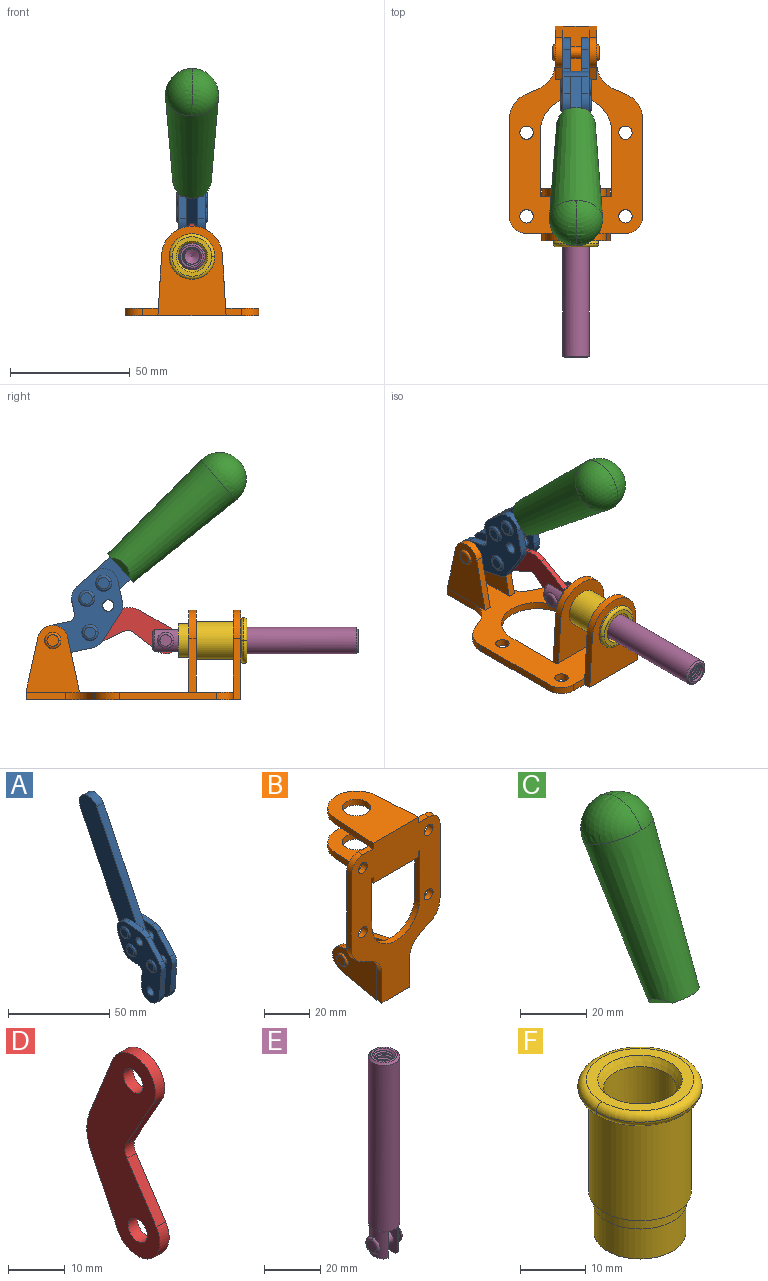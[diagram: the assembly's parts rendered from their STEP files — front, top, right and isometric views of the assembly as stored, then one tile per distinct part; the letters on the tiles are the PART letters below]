
ASSEMBLY  parts=6 mates=6
PART A: 59 faces, bbox 12.9x60.2x99.6 mm
  f0: torus R=2.39mm, axis (-1,0,0), area 14.9mm2, adj f20,f43,f51
  f1: torus R=2.39mm, axis (-1,0,0), area 14.9mm2, adj f19,f42,f51
  f2: torus R=2.39mm, axis (-1,0,0), area 14.9mm2, adj f18,f35,f51
  f3: torus R=2.39mm, axis (-1,0,0), area 14.9mm2, adj f14,f17,f23
  f4: torus R=2.39mm, axis (-1,0,0), area 14.9mm2, adj f13,f16,f23
  f5: torus R=2.39mm, axis (-1,0,0), area 14.9mm2, adj f12,f15,f23
  f6: cylinder r=2.39mm len=4.78mm, axis (1,0,0), area 46.5mm2, adj f48,f50,f51
  f7: cylinder r=2.39mm len=4.78mm, axis (1,0,0), area 46.5mm2, adj f50,f51
  f8: cylinder r=6.35mm len=12.68mm, axis (1,0,0), area 61.8mm2, adj f38,f39,f50,f51
  f9: cylinder r=2.39mm len=4.78mm, axis (-1,0,0), area 70.5mm2, adj f46,f50
  f10: cylinder r=2.39mm len=4.78mm, axis (-1,0,0), area 46.5mm2, adj f23,f45,f46
  f11: cylinder r=2.39mm len=4.78mm, axis (-1,0,0), area 46.5mm2, adj f23,f46
  f12: plane 4.78x4.78mm, normal (1,0,0), area 17.9mm2, adj f5,f15
  f13: plane 4.78x4.78mm, normal (1,0,0), area 17.9mm2, adj f4,f16
  f14: plane 4.78x4.78mm, normal (1,0,0), area 17.9mm2, adj f3,f17
  f15: torus R=2.39mm, axis (-1,0,0), area 14.9mm2, adj f5,f12,f23
  f16: torus R=2.39mm, axis (-1,0,0), area 14.9mm2, adj f4,f13,f23
  f17: torus R=2.39mm, axis (-1,0,0), area 14.9mm2, adj f3,f14,f23
  f18: plane 4.78x4.78mm, normal (-1,0,0), area 17.9mm2, adj f2,f35
  f19: plane 4.78x4.78mm, normal (-1,0,0), area 17.9mm2, adj f1,f42
  f20: plane 4.78x4.78mm, normal (-1,0,0), area 17.9mm2, adj f0,f43
  f21: plane 2.26x0.2mm, normal (1,0,0), area 0.2mm2, adj f31,f44
  f22: plane 2.26x0.2mm, normal (-1,0,0), area 0.2mm2, adj f41,f44
  f23: plane 39.37x30.77mm, normal (1,0,0), area 565.5mm2, adj f3,f4,f5,f10,f11,f15,f16,f17
  f24: cylinder r=6.1mm len=4.15mm, axis (-1,0,0), area 14.7mm2, adj f23,f25,f32,f46
  f25: plane 10.25x9.01mm, normal (0,-0.75,0.66), area 42.3mm2, adj f23,f24,f26,f46
  f26: cylinder r=6.35mm len=4.64mm, axis (-1,0,0), area 15.6mm2, adj f23,f25,f27,f46
  f27: plane 15.84x3.1mm, normal (0,-1,-0.07), area 49.2mm2, adj f23,f26,f28,f46
  f28: cylinder r=6.35mm len=12.68mm, axis (-1,0,0), area 61.8mm2, adj f23,f27,f29,f46
  f29: plane 8.11x3.1mm, normal (0,1,0.07), area 25.2mm2, adj f23,f28,f30,f46
  f30: cylinder r=3.05mm len=3.25mm, axis (-1,0,0), area 14.8mm2, adj f23,f29,f31,f46
  f31: plane 5.99x3.1mm, normal (0,0.07,-1), area 18.6mm2, adj f21,f23,f30,f44,f46
  f32: plane 9.5x3.1mm, normal (0,-0.07,1), area 29.5mm2, adj f23,f24,f33,f46,f47
  f33: cylinder r=6.1mm len=8.63mm, axis (-1,0,0), area 39.1mm2, adj f23,f32,f34,f47
  f34: plane 8.65x3.96mm, normal (0,0.91,-0.42), area 29.5mm2, adj f23,f33,f44,f47
  f35: torus R=2.39mm, axis (-1,0,0), area 14.9mm2, adj f2,f18,f51
  f36: plane 10.25x9.01mm, normal (0,-0.75,0.66), area 42.3mm2, adj f37,f49,f50,f51
  f37: cylinder r=6.35mm len=4.64mm, axis (1,0,0), area 15.6mm2, adj f36,f38,f50,f51
  f38: plane 15.84x3.1mm, normal (0,-1,-0.07), area 49.2mm2, adj f8,f37,f50,f51
  f39: plane 8.11x3.1mm, normal (0,1,0.07), area 25.2mm2, adj f8,f40,f50,f51
  f40: cylinder r=3.05mm len=3.25mm, axis (1,0,0), area 14.8mm2, adj f39,f41,f50,f51
  f41: plane 5.99x3.1mm, normal (0,0.07,-1), area 18.6mm2, adj f22,f40,f44,f50,f51
  f42: torus R=2.39mm, axis (-1,0,0), area 14.9mm2, adj f1,f19,f51
  f43: torus R=2.39mm, axis (-1,0,0), area 14.9mm2, adj f0,f20,f51
  f44: cylinder r=6.35mm len=12.12mm, axis (-1,0,0), area 128.9mm2, adj f21,f22,f23,f31,f34,f41,f46,f47
  f45: plane 2.65x1.35mm, normal (1,0,0), area 1mm2, adj f10,f55
  f46: plane 39.08x20.42mm, normal (-1,0,0), area 412.5mm2, adj f9,f10,f11,f24,f25,f26,f27,f28
  f47: plane 77.62x39.82mm, normal (1,0,0), area 850mm2, adj f32,f33,f34,f44,f53,f54,f55
  f48: plane 2.65x1.35mm, normal (-1,0,0), area 1mm2, adj f6,f55
  f49: cylinder r=6.1mm len=4.15mm, axis (1,0,0), area 14.7mm2, adj f36,f50,f51,f56
  f50: plane 39.08x20.42mm, normal (1,0,0), area 412.5mm2, adj f6,f7,f8,f9,f36,f37,f38,f39
  f51: plane 39.37x30.77mm, normal (-1,0,0), area 565.5mm2, adj f0,f1,f2,f6,f7,f8,f35,f36
  f52: plane 8.65x3.96mm, normal (0,0.91,-0.42), area 29.5mm2, adj f44,f51,f57,f58
  f53: plane 68.49x33.4mm, normal (0,0.9,-0.44), area 358.1mm2, adj f44,f47,f54,f58
  f54: cylinder r=6.35mm len=12.06mm, axis (1,0,0), area 93.7mm2, adj f47,f53,f55,f58
  f55: plane 68.49x33.4mm, normal (0,-0.9,0.44), area 358.1mm2, adj f44,f45,f46,f47,f48,f50,f54,f58
  f56: plane 9.5x3.1mm, normal (0,-0.07,1), area 29.5mm2, adj f49,f50,f51,f57,f58
  f57: cylinder r=6.1mm len=8.63mm, axis (1,0,0), area 39.1mm2, adj f51,f52,f56,f58
  f58: plane 77.62x39.82mm, normal (-1,0,0), area 850mm2, adj f44,f52,f53,f54,f55,f56,f57
PART B: 55 faces, bbox 55.7x37.4x89.8 mm
  f0: torus R=2.41mm, axis (-1,0,0), area 15mm2, adj f11,f15,f25
  f1: torus R=2.41mm, axis (-1,0,0), area 15mm2, adj f10,f12,f22
  f2: cylinder r=2.78mm len=5.56mm, axis (0,-1,0), area 54.2mm2, adj f30,f54
  f3: cylinder r=14.99mm len=29.97mm, axis (0,-1,0), area 145.9mm2, adj f30,f49,f53,f54
  f4: cylinder r=2.78mm len=5.56mm, axis (0,-1,0), area 54.2mm2, adj f30,f54
  f5: cylinder r=2.78mm len=5.56mm, axis (0,-1,0), area 54.2mm2, adj f30,f54
  f6: cylinder r=2.78mm len=5.56mm, axis (0,-1,0), area 54.2mm2, adj f30,f54
  f7: cylinder r=6.35mm len=12.7mm, axis (0,0,1), area 123.6mm2, adj f27,f51
  f8: cylinder r=6.35mm len=12.7mm, axis (0,0,-1), area 124.7mm2, adj f21,f35
  f9: cylinder r=2.41mm len=11.18mm, axis (-1,0,0), area 169.4mm2, adj f16,f19
  f10: plane 4.83x4.83mm, normal (1,0,0), area 18.3mm2, adj f1,f12
  f11: plane 4.83x4.83mm, normal (-1,0,0), area 18.3mm2, adj f0,f15
  f12: torus R=2.41mm, axis (-1,0,0), area 15mm2, adj f1,f10,f22
  f13: cylinder r=6.35mm len=12.41mm, axis (1,0,0), area 53.4mm2, adj f18,f19,f22,f23
  f14: cylinder r=6.35mm len=12.41mm, axis (-1,0,0), area 53.4mm2, adj f16,f17,f24,f25
  f15: torus R=2.41mm, axis (-1,0,0), area 15mm2, adj f0,f11,f25
  f16: plane 27.86x22.35mm, normal (1,0,0), area 425.4mm2, adj f9,f14,f17,f24,f30
  f17: plane 22.86x4.97mm, normal (0,0.21,0.98), area 72.5mm2, adj f14,f16,f25,f30
  f18: plane 22.86x4.97mm, normal (0,0.21,0.98), area 72.5mm2, adj f13,f19,f22,f30
  f19: plane 27.86x22.35mm, normal (-1,0,0), area 425.4mm2, adj f9,f13,f18,f23,f30
  f20: cylinder r=12.7mm len=25.35mm, axis (0,0,-1), area 119.8mm2, adj f21,f34,f35,f36
  f21: plane 34.21x28.07mm, normal (0,0,-1), area 702.4mm2, adj f8,f20,f30,f34,f36
  f22: plane 27.96x22.45mm, normal (1,0,0), area 407.2mm2, adj f1,f12,f13,f18,f23,f30,f42,f43
  f23: plane 22.86x4.97mm, normal (0,0.21,-0.98), area 72.5mm2, adj f13,f19,f22,f44
  f24: plane 22.86x4.97mm, normal (0,0.21,-0.98), area 72.5mm2, adj f14,f16,f25,f44
  f25: plane 27.86x22.35mm, normal (-1,0,0), area 407.1mm2, adj f0,f14,f15,f17,f24,f30,f45,f46
  f26: plane 3.1x0.95mm, normal (0,0,-1), area 2.7mm2, adj f30,f49,f50,f54
  f27: plane 34.21x28.07mm, normal (0,0,1), area 702.4mm2, adj f7,f28,f30,f50,f52
  f28: cylinder r=12.7mm len=25.35mm, axis (0,0,1), area 118.8mm2, adj f27,f50,f51,f52
  f29: plane 3.1x0.95mm, normal (0,0,-1), area 2.7mm2, adj f30,f52,f53,f54
  f30: plane 86.54x55.63mm, normal (0,1,0), area 2362.9mm2, adj f2,f3,f4,f5,f6,f16,f17,f18
  f31: plane 40.56x3.1mm, normal (-1,0,0), area 125.7mm2, adj f30,f32,f48,f54
  f32: cylinder r=7.11mm len=7.11mm, axis (0,-1,0), area 34.6mm2, adj f30,f31,f33,f54
  f33: plane 6.67x3.1mm, normal (0,0,1), area 20.4mm2, adj f30,f32,f34,f54
  f34: plane 25.39x3.13mm, normal (-1,0.06,0), area 79.5mm2, adj f20,f21,f33,f35,f54
  f35: plane 37.31x28.45mm, normal (0,0,1), area 789.9mm2, adj f8,f20,f34,f36,f54
  f36: plane 25.39x3.13mm, normal (1,0.06,0), area 79.5mm2, adj f20,f21,f35,f37,f54
  f37: plane 6.67x3.1mm, normal (0,0,1), area 20.4mm2, adj f30,f36,f38,f54
  f38: cylinder r=7.11mm len=7.11mm, axis (0,-1,0), area 34.6mm2, adj f30,f37,f39,f54
  f39: plane 40.56x3.1mm, normal (1,0,0), area 125.7mm2, adj f30,f38,f40,f54
  f40: cylinder r=11.18mm len=10.16mm, axis (0,-1,0), area 39.5mm2, adj f30,f39,f41,f54
  f41: plane 6.09x3.1mm, normal (0.42,0,-0.91), area 20.8mm2, adj f30,f40,f42,f54
  f42: cylinder r=11.18mm len=9.41mm, axis (0,-1,0), area 37.2mm2, adj f22,f30,f41,f43,f54
  f43: plane 16.5x3.1mm, normal (1,0,0), area 51.1mm2, adj f22,f42,f44,f54
  f44: plane 17.37x3.1mm, normal (0,0,-1), area 53.8mm2, adj f23,f24,f30,f43,f45,f54
  f45: plane 16.5x3.1mm, normal (-1,0,0), area 51.1mm2, adj f25,f44,f46,f54
  f46: cylinder r=11.18mm len=9.41mm, axis (0,-1,0), area 37.2mm2, adj f25,f30,f45,f47,f54
  f47: plane 6.09x3.1mm, normal (-0.42,0,-0.91), area 20.8mm2, adj f30,f46,f48,f54
  f48: cylinder r=11.18mm len=10.16mm, axis (0,-1,0), area 39.5mm2, adj f30,f31,f47,f54
  f49: plane 26.54x3.1mm, normal (-1,0,0), area 82.3mm2, adj f3,f26,f30,f54
  f50: plane 25.39x3.1mm, normal (1,0.06,0), area 78.8mm2, adj f26,f27,f28,f51,f54
  f51: plane 37.31x28.45mm, normal (0,0,-1), area 789.9mm2, adj f7,f28,f50,f52,f54
  f52: plane 25.39x3.1mm, normal (-1,0.06,0), area 78.8mm2, adj f27,f28,f29,f51,f54
  f53: plane 26.54x3.1mm, normal (1,0,0), area 82.3mm2, adj f3,f29,f30,f54
  f54: plane 89.66x55.63mm, normal (0,-1,0), area 2678.5mm2, adj f2,f3,f4,f5,f6,f26,f29,f31
PART C: 11 faces, bbox 22.3x42.6x64.5 mm
  f0: sphere r=11.13mm, area 411.4mm2, adj f1,f8
  f1: cone r=11.11mm half-angle=3.3deg, axis (0,0.44,0.9), area 3251.8mm2, adj f0,f7,f8,f9,f10
  f2: cylinder r=6.16mm len=11.7mm, axis (1,0,0), area 89.5mm2, adj f3,f4,f5,f6
  f3: plane 60.23x36.75mm, normal (-1,0,0), area 763.6mm2, adj f2,f4,f6,f10
  f4: plane 51.37x25.05mm, normal (0,0.9,-0.44), area 264.2mm2, adj f2,f3,f5,f10
  f5: plane 60.23x36.75mm, normal (1,0,0), area 763.6mm2, adj f2,f4,f6,f10
  f6: plane 51.37x25.05mm, normal (0,-0.9,0.44), area 264.2mm2, adj f2,f3,f5,f10
  f7: plane 9.95x5.95mm, normal (0.71,-0.31,-0.64), area 25.8mm2, adj f1,f10
  f8: sphere r=11.13mm, area 411.4mm2, adj f0,f1
  f9: plane 9.95x5.95mm, normal (-0.71,-0.31,-0.64), area 25.8mm2, adj f1,f10
  f10: plane 14.27x11.38mm, normal (0,-0.44,-0.9), area 106.7mm2, adj f1,f3,f4,f5,f6,f7,f9
PART D: 12 faces, bbox 2.3x18.2x42.8 mm
  f0: cylinder r=2.4mm len=4.8mm, axis (1,0,0), area 34.9mm2, adj f4,f11
  f1: cylinder r=10.41mm len=8.47mm, axis (1,0,0), area 20.2mm2, adj f4,f9,f10,f11
  f2: cylinder r=3.05mm len=3.16mm, axis (1,0,0), area 7.7mm2, adj f4,f6,f7,f11
  f3: cylinder r=2.4mm len=4.8mm, axis (1,0,0), area 34.9mm2, adj f4,f11
  f4: plane 42.81x18.23mm, normal (-1,0,0), area 414.1mm2, adj f0,f1,f2,f3,f5,f6,f7,f8
  f5: cylinder r=5.54mm len=10.67mm, axis (1,0,0), area 41.8mm2, adj f4,f6,f10,f11
  f6: plane 11.66x6.53mm, normal (0,-0.87,-0.49), area 30.9mm2, adj f2,f4,f5,f11
  f7: plane 11.17x7.33mm, normal (0,-0.84,0.55), area 30.9mm2, adj f2,f4,f8,f11
  f8: cylinder r=5.54mm len=10.51mm, axis (1,0,0), area 41.8mm2, adj f4,f7,f9,f11
  f9: plane 13.67x6.67mm, normal (0,0.9,-0.44), area 35.1mm2, adj f1,f4,f8,f11
  f10: plane 14.1x5.7mm, normal (0,0.93,0.37), area 35.1mm2, adj f1,f4,f5,f11
  f11: plane 42.81x18.23mm, normal (1,0,0), area 414.1mm2, adj f0,f1,f2,f3,f5,f6,f7,f8
PART E: 48 faces, bbox 12.6x11.1x86.1 mm
  f0: torus R=2.41mm, axis (-1,0,0), area 15mm2, adj f30,f32,f34
  f1: torus R=2.41mm, axis (-1,0,0), area 15mm2, adj f29,f31,f33
  f2: cylinder r=5.54mm len=72.39mm, axis (0,0,1), area 2518.5mm2, adj f3,f4,f42,f43
  f3: cone r=5.54mm half-angle=45deg, axis (0,0,1), area 7.6mm2, adj f2,f5,f41
  f4: cone r=5.54mm half-angle=45deg, axis (0,0,-1), area 34.9mm2, adj f2,f39
  f5: cylinder r=5.08mm len=11.48mm, axis (0,0,1), area 108.3mm2, adj f3,f7,f8,f41
  f6: cylinder r=2.41mm len=4.83mm, axis (-1,0,0), area 71.2mm2, adj f40,f41
  f7: cylinder r=2.41mm len=4.83mm, axis (-1,0,0), area 7.6mm2, adj f5,f34
  f8: cone r=5.08mm half-angle=45deg, axis (0,0,1), area 10.6mm2, adj f5,f37,f41
  f9: cone r=3.98mm half-angle=45deg, axis (0,0,1), area 17.6mm2, adj f27,f39,f45,f46,f47
  f10: cylinder r=2.41mm len=4.83mm, axis (-1,0,0), area 7.6mm2, adj f33,f38
  f11: cylinder r=3.2mm len=6.4mm, axis (0,0,1), area 78.4mm2, adj f12,f28,f44,f45,f47
  f12: cylinder r=3.2mm len=6.4mm, axis (0,0,1), area 10.5mm2, adj f11,f13,f45,f47
  f13: cylinder r=3.2mm len=6.4mm, axis (0,0,1), area 10.5mm2, adj f12,f14,f45,f47
  f14: cylinder r=3.2mm len=6.4mm, axis (0,0,1), area 10.5mm2, adj f13,f15,f45,f47
  f15: cylinder r=3.2mm len=6.4mm, axis (0,0,1), area 10.5mm2, adj f14,f16,f45,f47
  f16: cylinder r=3.2mm len=6.4mm, axis (0,0,1), area 10.5mm2, adj f15,f17,f45,f47
  f17: cylinder r=3.2mm len=6.4mm, axis (0,0,1), area 10.5mm2, adj f16,f18,f45,f47
  f18: cylinder r=3.2mm len=6.4mm, axis (0,0,1), area 10.5mm2, adj f17,f19,f45,f47
  f19: cylinder r=3.2mm len=6.4mm, axis (0,0,1), area 10.5mm2, adj f18,f20,f45,f47
  f20: cylinder r=3.2mm len=6.4mm, axis (0,0,1), area 10.5mm2, adj f19,f21,f45,f47
  f21: cylinder r=3.2mm len=6.4mm, axis (0,0,1), area 10.5mm2, adj f20,f22,f45,f47
  f22: cylinder r=3.2mm len=6.4mm, axis (0,0,1), area 10.5mm2, adj f21,f23,f45,f47
  f23: cylinder r=3.2mm len=6.4mm, axis (0,0,1), area 10.5mm2, adj f22,f24,f45,f47
  f24: cylinder r=3.2mm len=6.4mm, axis (0,0,1), area 10.5mm2, adj f23,f25,f45,f47
  f25: cylinder r=3.2mm len=6.4mm, axis (0,0,1), area 10.5mm2, adj f24,f26,f45,f47
  f26: cylinder r=3.2mm len=6.4mm, axis (0,0,1), area 10.5mm2, adj f25,f27,f45,f47
  f27: cylinder r=3.2mm len=6.4mm, axis (0,0,1), area 7.4mm2, adj f9,f26,f45,f47
  f28: cone r=3.2mm half-angle=60deg, axis (0,0,1), area 37.2mm2, adj f11
  f29: plane 4.83x4.83mm, normal (-1,0,0), area 18.3mm2, adj f1,f31
  f30: plane 4.83x4.83mm, normal (1,0,0), area 18.3mm2, adj f0,f32
  f31: torus R=2.41mm, axis (-1,0,0), area 15mm2, adj f1,f29,f33
  f32: torus R=2.41mm, axis (-1,0,0), area 15mm2, adj f0,f30,f34
  f33: plane 6.83x6.83mm, normal (1,0,0), area 18.3mm2, adj f1,f10,f31
  f34: plane 6.83x6.83mm, normal (-1,0,0), area 18.3mm2, adj f0,f7,f32
  f35: cone r=5.08mm half-angle=45deg, axis (0,0,1), area 10.6mm2, adj f36,f38,f40
  f36: plane 7.25x1.97mm, normal (0,0,-1), area 10mm2, adj f35,f40
  f37: plane 7.25x1.97mm, normal (0,0,-1), area 10mm2, adj f8,f41
  f38: cylinder r=5.08mm len=11.48mm, axis (0,0,1), area 108.3mm2, adj f10,f35,f40,f42
  f39: plane 9.55x9.55mm, normal (0,0,1), area 22mm2, adj f4,f9
  f40: plane 12.76x10.09mm, normal (1,0,0), area 95.7mm2, adj f6,f35,f36,f38,f42,f43
  f41: plane 12.76x10.09mm, normal (-1,0,0), area 95.7mm2, adj f3,f5,f6,f8,f37,f43
  f42: cone r=5.54mm half-angle=45deg, axis (0,0,1), area 7.6mm2, adj f2,f38,f40
  f43: plane 11.07x4.7mm, normal (0,0,-1), area 50.4mm2, adj f2,f40,f41
  f44: plane 0.89x0.62mm, normal (-1,0,0), area 0.3mm2, adj f11,f45,f46,f47
  f45: bspline ~24.8x7.63mm, area 266.6mm2, adj f9,f11,f12,f13,f14,f15,f16,f17
  f46: bspline ~24.87x7.63mm, area 73.6mm2, adj f9,f44,f45,f47
  f47: bspline ~24.98x7.63mm, area 272.5mm2, adj f9,f11,f12,f13,f14,f15,f16,f17
PART F: 15 faces, bbox 20.6x20.6x28.7 mm
  f0: torus R=8.26mm, axis (0,0,1), area 56.8mm2, adj f1,f10,f12
  f1: torus R=8.26mm, axis (0,0,1), area 56.8mm2, adj f0,f6,f13
  f2: cylinder r=5.59mm len=25.91mm, axis (0,0,1), area 909.6mm2, adj f3,f4
  f3: cone r=6.86mm half-angle=45deg, axis (0,0,-1), area 70.2mm2, adj f2,f14
  f4: cone r=6.47mm half-angle=30deg, axis (0,0,1), area 66.7mm2, adj f2,f13
  f5: cylinder r=7.04mm len=14.07mm, axis (0,0,1), area 252.6mm2, adj f11,f14
  f6: torus R=8.26mm, axis (0,0,1), area 56.8mm2, adj f1,f12,f13
  f7: cylinder r=7.16mm len=14.33mm, axis (0,0,1), area 91.5mm2, adj f9,f11
  f8: cylinder r=7.86mm len=18.42mm, axis (0,0,1), area 909.6mm2, adj f9,f10
  f9: plane 15.72x15.72mm, normal (0,0,-1), area 33mm2, adj f7,f8
  f10: plane 16.51x16.51mm, normal (0,0,-1), area 19.9mm2, adj f0,f8,f12
  f11: plane 14.33x14.33mm, normal (0,0,-1), area 5.7mm2, adj f5,f7
  f12: torus R=8.26mm, axis (0,0,1), area 56.8mm2, adj f0,f6,f10
  f13: plane 16.51x16.51mm, normal (0,0,1), area 82.7mm2, adj f1,f4,f6
  f14: plane 14.07x14.07mm, normal (0,0,-1), area 7.8mm2, adj f3,f5
PLACE A rot(axis=(1,0,0),74.1deg) t=(0,-4.28,9.74)mm
PLACE B rot(axis=(1,0,0),90deg) t=(0,1.23,0)mm fixed
PLACE C rot(axis=(1,0,0),74.1deg) t=(0,-4.28,9.74)mm
PLACE D rot(axis=(1,0,0),97.9deg) t=(0,4.93,2.37)mm
PLACE E rot(axis=(1,0,0),90deg) t=(0,1.68,0)mm
PLACE F rot(axis=(1,0,0),90deg) t=(0,1.23,0)mm
MATE revolute D.f5 <-> E.f6  axis (1,0,0) through (0,-13.79,24.61)mm
MATE fastened A.f54 <-> C.f2  axis (1,0,0) through (0,-37.49,93.07)mm
MATE fastened B.f7 <-> F.f2  axis (0,-1,0) through (0,-45.16,24.61)mm
MATE revolute D.f3 <-> A.f4  axis (1,0,0) through (0,17.79,27.89)mm
MATE slider F.f2 <-> E.f2  axis (0,-1,0) through (0,-35.95,24.61)mm
MATE revolute A.f7 <-> B.f0  axis (-1,0,0) through (0,33.32,24.61)mm
